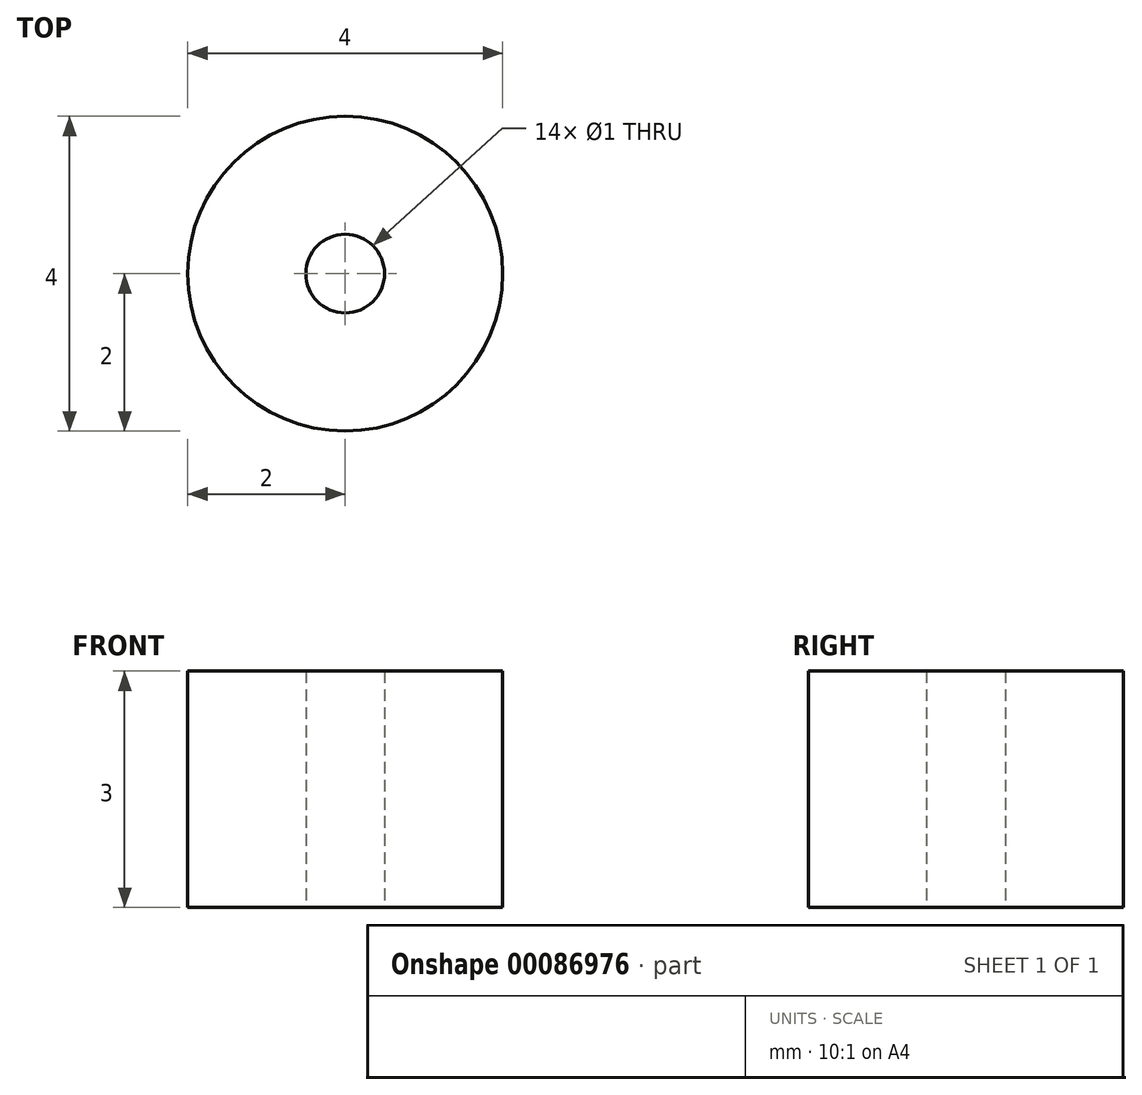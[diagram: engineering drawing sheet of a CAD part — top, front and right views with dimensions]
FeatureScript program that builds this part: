
annotation { "Feature Type Name" : "Feature", "Feature Type Description" : "" }
export const myFeature = defineFeature(function(context is Context, id is Id, definition is map)
    precondition{}
    {
        {
            var Q0;
            Q0=qCreatedBy(makeId("Top.planeOp"),FACE);
            var sketch = newSketch(context, id + "F0", { "sketchPlane" : qUnion([Q0])});
            skCircle(sketch, "E0", {"center": v(0, 0) * mm, "radius": 2 * mm});
            skCircle(sketch, "E1", {"center": v(0, 0) * mm, "radius": 0.5 * mm});
            skSolve(sketch);
        }
        {
            var Q0;
            Q0 = qSketchRegion(id + "F0", true);
            extrude(context, id + "F1", {"entities" : qUnion([Q0]), "depth" : 3 * mm});
        }
    });
